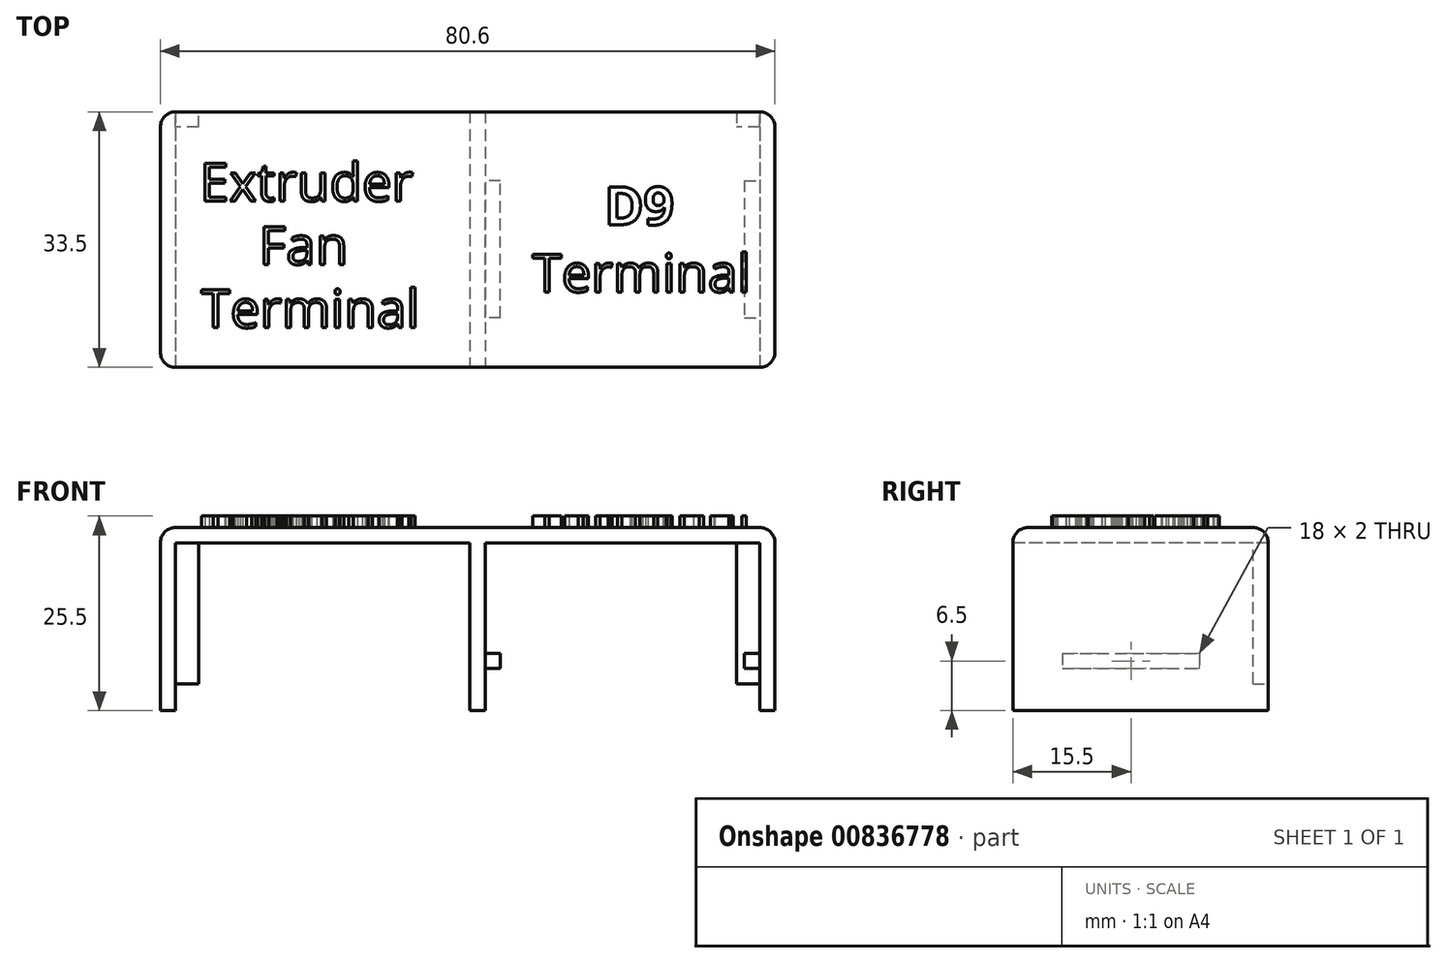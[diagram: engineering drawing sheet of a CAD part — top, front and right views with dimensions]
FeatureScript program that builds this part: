
annotation { "Feature Type Name" : "Feature", "Feature Type Description" : "" }
export const myFeature = defineFeature(function(context is Context, id is Id, definition is map)
    precondition{}
    {
        {
            var Q0;
            Q0=qCreatedBy(makeId("Front.planeOp"),FACE);
            var sketch = newSketch(context, id + "F0", { "sketchPlane" : qUnion([Q0])});
            skLineSegment(sketch, "E0", {"start": v(0, 0) * mm, "end": v(0, 24) * mm});
            skLineSegment(sketch, "E1", {"start": v(0, 24) * mm, "end": v(-80.6, 24) * mm});
            skLineSegment(sketch, "E2", {"start": v(-80.6, 24) * mm, "end": v(-80.6, 0) * mm});
            skLineSegment(sketch, "E3", {"start": v(-80.6, 0) * mm, "end": v(-78.6, 0) * mm});
            skLineSegment(sketch, "E4", {"start": v(-78.6, 0) * mm, "end": v(-78.6, 22) * mm});
            skLineSegment(sketch, "E5", {"start": v(-78.6, 22) * mm, "end": v(-40, 22) * mm});
            skLineSegment(sketch, "E6", {"start": v(-40, 22) * mm, "end": v(-40, 0) * mm});
            skLineSegment(sketch, "E7", {"start": v(-40, 0) * mm, "end": v(-38, 0) * mm});
            skLineSegment(sketch, "E8", {"start": v(-38, 0) * mm, "end": v(-38, 22) * mm});
            skLineSegment(sketch, "E9", {"start": v(-38, 22) * mm, "end": v(-2, 22) * mm});
            skLineSegment(sketch, "E10", {"start": v(-2, 22) * mm, "end": v(-2, 0) * mm});
            skLineSegment(sketch, "E11", {"start": v(-2, 0) * mm, "end": v(0, 0) * mm});
            skSolve(sketch);
        }
        {
            var Q0;
            Q0=makeQuery(id+"F0.imprint","IMPRINT",FACE,{"disambiguationData":[TD([[makeQuery(id+"F0.imprint","IMPRINT",EDGE,{"derivedFrom":sQuery(id+"F0.wireOp",EDGE,"E0")}),1.0]])]});
            extrude(context, id + "F1", {"entities" : qUnion([Q0]), "oppositeDirection" : true, "depth" : 33.5 * mm, "offsetDistance" : 25 * mm});
        }
        {
            var Q0;
            Q0=makeQuery(id+"F1.opExtrude","SWEPT_FACE",FACE,{"disambiguationData":[OSD([sQuery(id+"F0.wireOp",EDGE,"E8")])]});
            var sketch = newSketch(context, id + "F2", { "sketchPlane" : qUnion([Q0])});
            skLineSegment(sketch, "E12.bottom", {"start": v(6.5, 7.5) * mm, "end": v(24.5, 7.5) * mm});
            skLineSegment(sketch, "E12.top", {"start": v(6.5, 5.5) * mm, "end": v(24.5, 5.5) * mm});
            skLineSegment(sketch, "E12.left", {"start": v(6.5, 7.5) * mm, "end": v(6.5, 5.5) * mm});
            skLineSegment(sketch, "E12.right", {"start": v(24.5, 7.5) * mm, "end": v(24.5, 5.5) * mm});
            skSolve(sketch);
        }
        {
            var Q0;
            Q0=makeQuery(id+"F2.imprint","IMPRINT",FACE,{"disambiguationData":[TD([[makeQuery(id+"F2.imprint","IMPRINT",EDGE,{"derivedFrom":sQuery(id+"F2.wireOp",EDGE,"E12.bottom")}),-1.0]])]});
            extrude(context, id + "F3", {"entities" : qUnion([Q0]), "operationType" : NewBodyOperationType.ADD, "depth" : 2 * mm, "offsetDistance" : 25 * mm});
        }
        {
            var Q0;
            Q0=makeQuery(id+"F1.opExtrude","SWEPT_FACE",FACE,{"disambiguationData":[OSD([sQuery(id+"F0.wireOp",EDGE,"E10")])]});
            var sketch = newSketch(context, id + "F4", { "sketchPlane" : qUnion([Q0])});
            skLineSegment(sketch, "E13.bottom", {"start": v(-24.5, 7.5) * mm, "end": v(-6.5, 7.5) * mm});
            skLineSegment(sketch, "E13.top", {"start": v(-24.5, 5.5) * mm, "end": v(-6.5, 5.5) * mm});
            skLineSegment(sketch, "E13.left", {"start": v(-24.5, 7.5) * mm, "end": v(-24.5, 5.5) * mm});
            skLineSegment(sketch, "E13.right", {"start": v(-6.5, 7.5) * mm, "end": v(-6.5, 5.5) * mm});
            skSolve(sketch);
        }
        {
            var Q0;
            Q0=makeQuery(id+"F4.imprint","IMPRINT",FACE,{"disambiguationData":[TD([[makeQuery(id+"F4.imprint","IMPRINT",EDGE,{"derivedFrom":sQuery(id+"F4.wireOp",EDGE,"E13.bottom")}),-1.0]])]});
            extrude(context, id + "F5", {"entities" : qUnion([Q0]), "operationType" : NewBodyOperationType.ADD, "depth" : 2 * mm, "offsetDistance" : 25 * mm});
        }
        {
            var Q0;
            Q0=makeQuery(id+"F1.opExtrude","SWEPT_FACE",FACE,{"disambiguationData":[OSD([sQuery(id+"F0.wireOp",EDGE,"E1")])]});
            var sketch = newSketch(context, id + "F6", { "sketchPlane" : qUnion([Q0])});
            skText(sketch, "E14", { "text": "D9\n", "fontName": "OpenSans-Bold.ttf"});
            skText(sketch, "E15", { "text": "Terminal\n", "fontName": "OpenSans-Regular.ttf"});
            skText(sketch, "E16", { "text": "Extruder\n", "fontName": "OpenSans-Regular.ttf"});
            skText(sketch, "E17", { "text": "Fan\n\n", "fontName": "OpenSans-Regular.ttf"});
            skText(sketch, "E18", { "text": "Terminal", "fontName": "OpenSans-Regular.ttf"});
            const initialGuessF6  = {"E14": [-0.02236, 0.0187, 1, 0, 0.005], "E15": [-0.03182, 0.00989, 1, 0, 0.005], "E16": [-0.07545, 0.0218, 1, 0, 0.005], "E17": [-0.0677, 0.0135, 1, 0, 0.005], "E18": [-0.07527, 0.0052, 1, 0, 0.005]};
            skSetInitialGuess(sketch, initialGuessF6);
            skSolve(sketch);
        }
        {
            var Q0;
            Q0 = qSketchRegion(id + "F6", true);
            extrude(context, id + "F7", {"entities" : qUnion([Q0]), "operationType" : NewBodyOperationType.ADD, "depth" : 1.5 * mm, "offsetDistance" : 25 * mm});
        }
        {
            var Q0;
            Q0=makeQuery(id+"F1.opExtrude","SWEPT_FACE",FACE,{"disambiguationData":[OSD([sQuery(id+"F0.wireOp",EDGE,"E10")])]});
            var sketch = newSketch(context, id + "F8", { "sketchPlane" : qUnion([Q0])});
            skLineSegment(sketch, "E19.bottom", {"start": v(-33.5, 0) * mm, "end": v(-31.5, 0) * mm});
            skLineSegment(sketch, "E19.top", {"start": v(-33.5, 22) * mm, "end": v(-31.5, 22) * mm});
            skLineSegment(sketch, "E19.left", {"start": v(-33.5, 0) * mm, "end": v(-33.5, 22) * mm});
            skLineSegment(sketch, "E19.right", {"start": v(-31.5, 0) * mm, "end": v(-31.5, 22) * mm});
            skSolve(sketch);
        }
        {
            var Q0;
            Q0=makeQuery(id+"F8.imprint","IMPRINT",FACE,{"disambiguationData":[TD([[makeQuery(id+"F8.imprint","IMPRINT",EDGE,{"derivedFrom":sQuery(id+"F8.wireOp",EDGE,"E19.bottom")}),1.0]])]});
            extrude(context, id + "F9", {"entities" : qUnion([Q0]), "operationType" : NewBodyOperationType.ADD, "depth" : 3 * mm, "offsetDistance" : 25 * mm});
        }
        {
            var Q0;
            Q0=makeQuery(id+"F1.opExtrude","SWEPT_FACE",FACE,{"disambiguationData":[OSD([sQuery(id+"F0.wireOp",EDGE,"E4")])]});
            var sketch = newSketch(context, id + "F10", { "sketchPlane" : qUnion([Q0])});
            skLineSegment(sketch, "E20.bottom", {"start": v(33.5, 22) * mm, "end": v(31.5, 22) * mm});
            skLineSegment(sketch, "E20.top", {"start": v(33.5, 0) * mm, "end": v(31.5, 0) * mm});
            skLineSegment(sketch, "E20.left", {"start": v(33.5, 22) * mm, "end": v(33.5, 0) * mm});
            skLineSegment(sketch, "E20.right", {"start": v(31.5, 22) * mm, "end": v(31.5, 0) * mm});
            skSolve(sketch);
        }
        {
            var Q0;
            Q0=makeQuery(id+"F10.imprint","IMPRINT",FACE,{"disambiguationData":[TD([[makeQuery(id+"F10.imprint","IMPRINT",EDGE,{"derivedFrom":sQuery(id+"F10.wireOp",EDGE,"E20.bottom")}),1.0]])]});
            extrude(context, id + "F11", {"entities" : qUnion([Q0]), "operationType" : NewBodyOperationType.ADD, "depth" : 3 * mm, "offsetDistance" : 25 * mm});
        }
        {
            var Q0;
            Q0=makeQuery(id+"F11.boolean.opBoolean","MERGE",FACE,{"derivedFrom":[makeQuery(id+"F9.boolean.opBoolean","MERGE",FACE,{"derivedFrom":[makeQuery(id+"F1.opExtrude","CAP_FACE",FACE,{"disambiguationData":[OSD([sQuery(id+"F0.wireOp",EDGE,"E0"),sQuery(id+"F0.wireOp",EDGE,"E1"),sQuery(id+"F0.wireOp",EDGE,"E2"),sQuery(id+"F0.wireOp",EDGE,"E3"),sQuery(id+"F0.wireOp",EDGE,"E4"),sQuery(id+"F0.wireOp",EDGE,"E5"),sQuery(id+"F0.wireOp",EDGE,"E6"),sQuery(id+"F0.wireOp",EDGE,"E7"),sQuery(id+"F0.wireOp",EDGE,"E8"),sQuery(id+"F0.wireOp",EDGE,"E9"),sQuery(id+"F0.wireOp",EDGE,"E10"),sQuery(id+"F0.wireOp",EDGE,"E11")])],"isStart":false}),makeQuery(id+"F9.opExtrude","SWEPT_FACE",FACE,{"disambiguationData":[OSD([sQuery(id+"F8.wireOp",EDGE,"E19.left")])]})]}),makeQuery(id+"F11.opExtrude","SWEPT_FACE",FACE,{"disambiguationData":[OSD([sQuery(id+"F10.wireOp",EDGE,"E20.left")])]})]});
            var sketch = newSketch(context, id + "F12", { "sketchPlane" : qUnion([Q0])});
            skLineSegment(sketch, "E21.bottom", {"start": v(75.6, 0) * mm, "end": v(78.6, 0) * mm});
            skLineSegment(sketch, "E21.top", {"start": v(75.6, 3.5) * mm, "end": v(78.6, 3.5) * mm});
            skLineSegment(sketch, "E21.left", {"start": v(75.6, 0) * mm, "end": v(75.6, 3.5) * mm});
            skLineSegment(sketch, "E21.right", {"start": v(78.6, 0) * mm, "end": v(78.6, 3.5) * mm});
            skSolve(sketch);
        }
        {
            var Q0;
            Q0=makeQuery(id+"F12.imprint","IMPRINT",FACE,{"disambiguationData":[TD([[makeQuery(id+"F12.imprint","IMPRINT",EDGE,{"derivedFrom":sQuery(id+"F12.wireOp",EDGE,"E21.bottom")}),-1.0]])]});
            extrude(context, id + "F13", {"entities" : qUnion([Q0]), "operationType" : NewBodyOperationType.REMOVE, "endBound" : BoundingType.UP_TO_NEXT, "oppositeDirection" : true, "depth" : 25 * mm, "offsetDistance" : 25 * mm});
        }
        {
            var Q0;
            Q0=makeQuery(id+"F11.boolean.opBoolean","MERGE",FACE,{"derivedFrom":[makeQuery(id+"F9.boolean.opBoolean","MERGE",FACE,{"derivedFrom":[makeQuery(id+"F1.opExtrude","CAP_FACE",FACE,{"disambiguationData":[OSD([sQuery(id+"F0.wireOp",EDGE,"E0"),sQuery(id+"F0.wireOp",EDGE,"E1"),sQuery(id+"F0.wireOp",EDGE,"E2"),sQuery(id+"F0.wireOp",EDGE,"E3"),sQuery(id+"F0.wireOp",EDGE,"E4"),sQuery(id+"F0.wireOp",EDGE,"E5"),sQuery(id+"F0.wireOp",EDGE,"E6"),sQuery(id+"F0.wireOp",EDGE,"E7"),sQuery(id+"F0.wireOp",EDGE,"E8"),sQuery(id+"F0.wireOp",EDGE,"E9"),sQuery(id+"F0.wireOp",EDGE,"E10"),sQuery(id+"F0.wireOp",EDGE,"E11")])],"isStart":false}),makeQuery(id+"F9.opExtrude","SWEPT_FACE",FACE,{"disambiguationData":[OSD([sQuery(id+"F8.wireOp",EDGE,"E19.left")])]})]}),makeQuery(id+"F11.opExtrude","SWEPT_FACE",FACE,{"disambiguationData":[OSD([sQuery(id+"F10.wireOp",EDGE,"E20.left")])]})]});
            var sketch = newSketch(context, id + "F14", { "sketchPlane" : qUnion([Q0])});
            skLineSegment(sketch, "E22.bottom", {"start": v(5, 0) * mm, "end": v(2, 0) * mm});
            skLineSegment(sketch, "E22.top", {"start": v(5, 3.5) * mm, "end": v(2, 3.5) * mm});
            skLineSegment(sketch, "E22.left", {"start": v(5, 0) * mm, "end": v(5, 3.5) * mm});
            skLineSegment(sketch, "E22.right", {"start": v(2, 0) * mm, "end": v(2, 3.5) * mm});
            skSolve(sketch);
        }
        {
            var Q0;
            Q0=makeQuery(id+"F14.imprint","IMPRINT",FACE,{"disambiguationData":[TD([[makeQuery(id+"F14.imprint","IMPRINT",EDGE,{"derivedFrom":sQuery(id+"F14.wireOp",EDGE,"E22.bottom")}),-1.0]])]});
            extrude(context, id + "F15", {"entities" : qUnion([Q0]), "operationType" : NewBodyOperationType.REMOVE, "endBound" : BoundingType.UP_TO_NEXT, "oppositeDirection" : true, "depth" : 25 * mm, "offsetDistance" : 25 * mm});
        }
        {
            var Q0;
            Q0=makeQuery(id+"F1.opExtrude","SWEPT_EDGE",EDGE,{"disambiguationData":[OSD([sQuery(id+"F0.wireOp",EDGE,"E1"),sQuery(id+"F0.wireOp",EDGE,"E2")])]});
            var Q1;
            Q1=makeQuery(id+"F1.opExtrude","SWEPT_EDGE",EDGE,{"disambiguationData":[OSD([sQuery(id+"F0.wireOp",EDGE,"E0"),sQuery(id+"F0.wireOp",EDGE,"E1")])]});
            var Q2;
            Q2=makeQuery(id+"F1.opExtrude","CAP_EDGE",EDGE,{"disambiguationData":[OSD([sQuery(id+"F0.wireOp",EDGE,"E0")])],"isStart":true});
            var Q3;
            Q3=makeQuery(id+"F1.opExtrude","CAP_EDGE",EDGE,{"disambiguationData":[OSD([sQuery(id+"F0.wireOp",EDGE,"E1")])],"isStart":true});
            var Q4;
            Q4=makeQuery(id+"F1.opExtrude","CAP_EDGE",EDGE,{"disambiguationData":[OSD([sQuery(id+"F0.wireOp",EDGE,"E2")])],"isStart":true});
            var Q5;
            Q5=makeQuery(id+"F1.opExtrude","CAP_EDGE",EDGE,{"disambiguationData":[OSD([sQuery(id+"F0.wireOp",EDGE,"E1")])],"isStart":false});
            var Q6;
            Q6=makeQuery(id+"F1.opExtrude","CAP_EDGE",EDGE,{"disambiguationData":[OSD([sQuery(id+"F0.wireOp",EDGE,"E2")])],"isStart":false});
            var Q7;
            Q7=makeQuery(id+"F1.opExtrude","CAP_EDGE",EDGE,{"disambiguationData":[OSD([sQuery(id+"F0.wireOp",EDGE,"E0")])],"isStart":false});
            fillet(context, id + "F16", {"entities" : qUnion([Q0, Q1, Q2, Q3, Q4, Q5, Q6, Q7]), "radius" : 2 * mm, "tangentPropagation" : true, "allowEdgeOverflow" : false});
        }
    });
